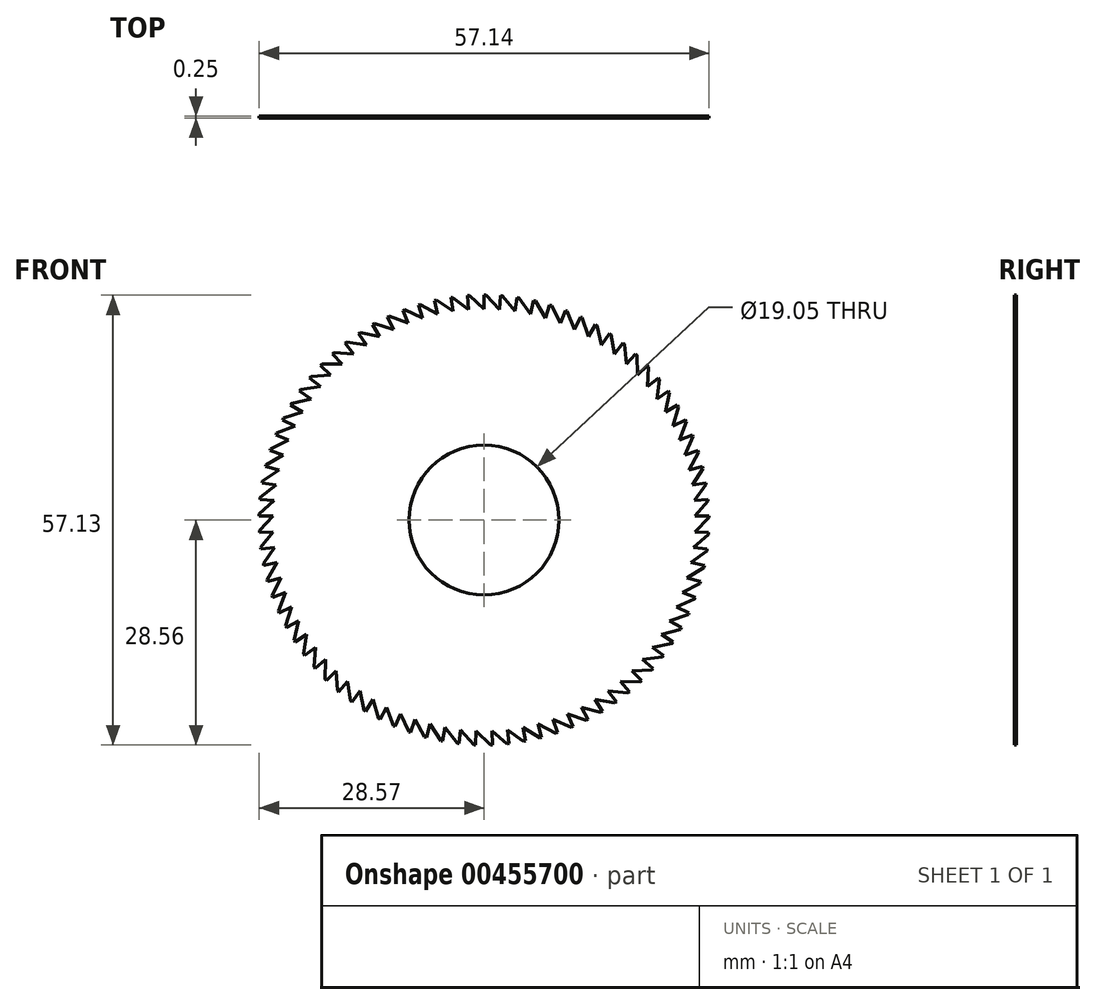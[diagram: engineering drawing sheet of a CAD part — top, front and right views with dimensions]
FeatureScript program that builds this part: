
annotation { "Feature Type Name" : "Feature", "Feature Type Description" : "" }
export const myFeature = defineFeature(function(context is Context, id is Id, definition is map)
    precondition{}
    {
        {
            var Q0;
            Q0=qCreatedBy(makeId("Front.planeOp"),FACE);
            var sketch = newSketch(context, id + "F0", { "sketchPlane" : qUnion([Q0])});
            skCircle(sketch, "E0", {"center": v(0, 0) * mm, "radius": 9.53 * mm});
            skLineSegment(sketch, "E1", {"start": v(0, 28.58) * mm, "end": v(0, 26.82) * mm});
            skLineSegment(sketch, "E2", {"start": v(0, 26.82) * mm, "end": v(-1.88, 28.51) * mm});
            skLineSegment(sketch, "E3.1.0", {"start": v(-1.98, 26.74) * mm, "end": v(-3.98, 28.3) * mm});
            skLineSegment(sketch, "E3.1.1", {"start": v(-2.11, 28.5) * mm, "end": v(-1.98, 26.74) * mm});
            skLineSegment(sketch, "E3.2.0", {"start": v(-3.95, 26.53) * mm, "end": v(-6.06, 27.93) * mm});
            skLineSegment(sketch, "E3.2.1", {"start": v(-4.2, 28.26) * mm, "end": v(-3.95, 26.53) * mm});
            skLineSegment(sketch, "E3.3.0", {"start": v(-5.9, 26.16) * mm, "end": v(-8.1, 27.4) * mm});
            skLineSegment(sketch, "E3.3.1", {"start": v(-6.28, 27.88) * mm, "end": v(-5.9, 26.16) * mm});
            skLineSegment(sketch, "E3.4.0", {"start": v(-7.81, 25.65) * mm, "end": v(-10.1, 26.73) * mm});
            skLineSegment(sketch, "E3.4.1", {"start": v(-8.33, 27.33) * mm, "end": v(-7.81, 25.65) * mm});
            skLineSegment(sketch, "E3.5.0", {"start": v(-9.69, 25) * mm, "end": v(-12.05, 25.9) * mm});
            skLineSegment(sketch, "E3.5.1", {"start": v(-10.32, 26.65) * mm, "end": v(-9.69, 25) * mm});
            skLineSegment(sketch, "E3.6.0", {"start": v(-11.5, 24.22) * mm, "end": v(-13.93, 24.95) * mm});
            skLineSegment(sketch, "E3.6.1", {"start": v(-12.26, 25.81) * mm, "end": v(-11.5, 24.22) * mm});
            skLineSegment(sketch, "E3.7.0", {"start": v(-13.27, 23.3) * mm, "end": v(-15.74, 23.85) * mm});
            skLineSegment(sketch, "E3.7.1", {"start": v(-14.13, 24.83) * mm, "end": v(-13.27, 23.3) * mm});
            skLineSegment(sketch, "E3.8.0", {"start": v(-14.95, 22.26) * mm, "end": v(-17.45, 22.62) * mm});
            skLineSegment(sketch, "E3.8.1", {"start": v(-15.93, 23.72) * mm, "end": v(-14.95, 22.26) * mm});
            skLineSegment(sketch, "E3.9.0", {"start": v(-16.55, 21.1) * mm, "end": v(-19.08, 21.27) * mm});
            skLineSegment(sketch, "E3.9.1", {"start": v(-17.64, 22.48) * mm, "end": v(-16.55, 21.1) * mm});
            skLineSegment(sketch, "E3.10.0", {"start": v(-18.07, 19.82) * mm, "end": v(-20.6, 19.8) * mm});
            skLineSegment(sketch, "E3.10.1", {"start": v(-19.25, 21.12) * mm, "end": v(-18.07, 19.82) * mm});
            skLineSegment(sketch, "E3.11.0", {"start": v(-19.48, 18.43) * mm, "end": v(-22, 18.23) * mm});
            skLineSegment(sketch, "E3.11.1", {"start": v(-20.76, 19.64) * mm, "end": v(-19.48, 18.43) * mm});
            skLineSegment(sketch, "E3.12.0", {"start": v(-20.79, 16.94) * mm, "end": v(-23.29, 16.56) * mm});
            skLineSegment(sketch, "E3.12.1", {"start": v(-22.15, 18.05) * mm, "end": v(-20.79, 16.94) * mm});
            skLineSegment(sketch, "E3.13.0", {"start": v(-21.98, 15.36) * mm, "end": v(-24.45, 14.8) * mm});
            skLineSegment(sketch, "E3.13.1", {"start": v(-23.42, 16.37) * mm, "end": v(-21.98, 15.36) * mm});
            skLineSegment(sketch, "E3.14.0", {"start": v(-23.06, 13.7) * mm, "end": v(-25.47, 12.95) * mm});
            skLineSegment(sketch, "E3.14.1", {"start": v(-24.57, 14.6) * mm, "end": v(-23.06, 13.7) * mm});
            skLineSegment(sketch, "E3.15.0", {"start": v(-24, 11.95) * mm, "end": v(-26.36, 11.03) * mm});
            skLineSegment(sketch, "E3.15.1", {"start": v(-25.58, 12.74) * mm, "end": v(-24, 11.95) * mm});
            skLineSegment(sketch, "E3.16.0", {"start": v(-24.82, 10.15) * mm, "end": v(-27.1, 9.05) * mm});
            skLineSegment(sketch, "E3.16.1", {"start": v(-26.45, 10.81) * mm, "end": v(-24.82, 10.15) * mm});
            skLineSegment(sketch, "E3.17.0", {"start": v(-25.5, 8.29) * mm, "end": v(-27.7, 7.03) * mm});
            skLineSegment(sketch, "E3.17.1", {"start": v(-27.18, 8.83) * mm, "end": v(-25.5, 8.29) * mm});
            skLineSegment(sketch, "E3.18.0", {"start": v(-26.05, 6.38) * mm, "end": v(-28.14, 4.96) * mm});
            skLineSegment(sketch, "E3.18.1", {"start": v(-27.75, 6.8) * mm, "end": v(-26.05, 6.38) * mm});
            skLineSegment(sketch, "E3.19.0", {"start": v(-26.45, 4.44) * mm, "end": v(-28.43, 2.87) * mm});
            skLineSegment(sketch, "E3.19.1", {"start": v(-28.18, 4.73) * mm, "end": v(-26.45, 4.44) * mm});
            skLineSegment(sketch, "E3.20.0", {"start": v(-26.7, 2.47) * mm, "end": v(-28.56, 0.76) * mm});
            skLineSegment(sketch, "E3.20.1", {"start": v(-28.45, 2.64) * mm, "end": v(-26.7, 2.47) * mm});
            skLineSegment(sketch, "E3.21.0", {"start": v(-26.81, 0.5) * mm, "end": v(-28.54, -1.35) * mm});
            skLineSegment(sketch, "E3.21.1", {"start": v(-28.57, 0.53) * mm, "end": v(-26.81, 0.5) * mm});
            skLineSegment(sketch, "E3.22.0", {"start": v(-26.78, -1.49) * mm, "end": v(-28.37, -3.45) * mm});
            skLineSegment(sketch, "E3.22.1", {"start": v(-28.53, -1.58) * mm, "end": v(-26.78, -1.49) * mm});
            skLineSegment(sketch, "E3.23.0", {"start": v(-26.6, -3.46) * mm, "end": v(-28.03, -5.54) * mm});
            skLineSegment(sketch, "E3.23.1", {"start": v(-28.34, -3.69) * mm, "end": v(-26.6, -3.46) * mm});
            skLineSegment(sketch, "E3.24.0", {"start": v(-26.27, -5.41) * mm, "end": v(-27.55, -7.6) * mm});
            skLineSegment(sketch, "E3.24.1", {"start": v(-27.99, -5.77) * mm, "end": v(-26.27, -5.41) * mm});
            skLineSegment(sketch, "E3.25.0", {"start": v(-25.8, -7.34) * mm, "end": v(-26.91, -9.6) * mm});
            skLineSegment(sketch, "E3.25.1", {"start": v(-27.48, -7.82) * mm, "end": v(-25.8, -7.34) * mm});
            skLineSegment(sketch, "E3.26.0", {"start": v(-25.18, -9.22) * mm, "end": v(-26.13, -11.57) * mm});
            skLineSegment(sketch, "E3.26.1", {"start": v(-26.83, -9.83) * mm, "end": v(-25.18, -9.22) * mm});
            skLineSegment(sketch, "E3.27.0", {"start": v(-24.43, -11.06) * mm, "end": v(-25.2, -13.47) * mm});
            skLineSegment(sketch, "E3.27.1", {"start": v(-26.03, -11.78) * mm, "end": v(-24.43, -11.06) * mm});
            skLineSegment(sketch, "E3.28.0", {"start": v(-23.55, -12.83) * mm, "end": v(-24.14, -15.3) * mm});
            skLineSegment(sketch, "E3.28.1", {"start": v(-25.1, -13.67) * mm, "end": v(-23.55, -12.83) * mm});
            skLineSegment(sketch, "E3.29.0", {"start": v(-22.54, -14.54) * mm, "end": v(-22.94, -17.03) * mm});
            skLineSegment(sketch, "E3.29.1", {"start": v(-24.01, -15.49) * mm, "end": v(-22.54, -14.54) * mm});
            skLineSegment(sketch, "E3.30.0", {"start": v(-21.4, -16.16) * mm, "end": v(-21.62, -18.68) * mm});
            skLineSegment(sketch, "E3.30.1", {"start": v(-22.8, -17.22) * mm, "end": v(-21.4, -16.16) * mm});
            skLineSegment(sketch, "E3.31.0", {"start": v(-20.15, -17.7) * mm, "end": v(-20.18, -20.23) * mm});
            skLineSegment(sketch, "E3.31.1", {"start": v(-21.47, -18.86) * mm, "end": v(-20.15, -17.7) * mm});
            skLineSegment(sketch, "E3.32.0", {"start": v(-18.79, -19.14) * mm, "end": v(-18.63, -21.66) * mm});
            skLineSegment(sketch, "E3.32.1", {"start": v(-20.02, -20.4) * mm, "end": v(-18.79, -19.14) * mm});
            skLineSegment(sketch, "E3.33.0", {"start": v(-17.32, -20.47) * mm, "end": v(-16.98, -22.98) * mm});
            skLineSegment(sketch, "E3.33.1", {"start": v(-18.46, -21.81) * mm, "end": v(-17.32, -20.47) * mm});
            skLineSegment(sketch, "E3.34.0", {"start": v(-15.76, -21.7) * mm, "end": v(-15.24, -24.17) * mm});
            skLineSegment(sketch, "E3.34.1", {"start": v(-16.8, -23.12) * mm, "end": v(-15.76, -21.7) * mm});
            skLineSegment(sketch, "E3.35.0", {"start": v(-14.12, -22.8) * mm, "end": v(-13.41, -25.23) * mm});
            skLineSegment(sketch, "E3.35.1", {"start": v(-15.04, -24.3) * mm, "end": v(-14.12, -22.8) * mm});
            skLineSegment(sketch, "E3.36.0", {"start": v(-12.4, -23.78) * mm, "end": v(-11.51, -26.15) * mm});
            skLineSegment(sketch, "E3.36.1", {"start": v(-13.2, -25.34) * mm, "end": v(-12.4, -23.78) * mm});
            skLineSegment(sketch, "E3.37.0", {"start": v(-10.6, -24.63) * mm, "end": v(-9.55, -26.93) * mm});
            skLineSegment(sketch, "E3.37.1", {"start": v(-11.3, -26.25) * mm, "end": v(-10.6, -24.63) * mm});
            skLineSegment(sketch, "E3.38.0", {"start": v(-8.76, -25.35) * mm, "end": v(-7.54, -27.56) * mm});
            skLineSegment(sketch, "E3.38.1", {"start": v(-9.33, -27) * mm, "end": v(-8.76, -25.35) * mm});
            skLineSegment(sketch, "E3.39.0", {"start": v(-6.86, -25.93) * mm, "end": v(-5.48, -28.04) * mm});
            skLineSegment(sketch, "E3.39.1", {"start": v(-7.31, -27.62) * mm, "end": v(-6.86, -25.93) * mm});
            skLineSegment(sketch, "E3.40.0", {"start": v(-4.93, -26.36) * mm, "end": v(-3.4, -28.37) * mm});
            skLineSegment(sketch, "E3.40.1", {"start": v(-5.25, -28.09) * mm, "end": v(-4.93, -26.36) * mm});
            skLineSegment(sketch, "E3.41.0", {"start": v(-2.97, -26.65) * mm, "end": v(-1.29, -28.55) * mm});
            skLineSegment(sketch, "E3.41.1", {"start": v(-3.16, -28.4) * mm, "end": v(-2.97, -26.65) * mm});
            skLineSegment(sketch, "E3.42.0", {"start": v(-1, -26.8) * mm, "end": v(0.82, -28.56) * mm});
            skLineSegment(sketch, "E3.42.1", {"start": v(-1.06, -28.56) * mm, "end": v(-1, -26.8) * mm});
            skLineSegment(sketch, "E3.43.0", {"start": v(1, -26.8) * mm, "end": v(2.93, -28.42) * mm});
            skLineSegment(sketch, "E3.43.1", {"start": v(1.06, -28.56) * mm, "end": v(1, -26.8) * mm});
            skLineSegment(sketch, "E3.44.0", {"start": v(2.97, -26.65) * mm, "end": v(5.02, -28.13) * mm});
            skLineSegment(sketch, "E3.44.1", {"start": v(3.16, -28.4) * mm, "end": v(2.97, -26.65) * mm});
            skLineSegment(sketch, "E3.45.0", {"start": v(4.93, -26.36) * mm, "end": v(7.09, -27.68) * mm});
            skLineSegment(sketch, "E3.45.1", {"start": v(5.25, -28.09) * mm, "end": v(4.93, -26.36) * mm});
            skLineSegment(sketch, "E3.46.0", {"start": v(6.86, -25.93) * mm, "end": v(9.11, -27.08) * mm});
            skLineSegment(sketch, "E3.46.1", {"start": v(7.31, -27.62) * mm, "end": v(6.86, -25.93) * mm});
            skLineSegment(sketch, "E3.47.0", {"start": v(8.76, -25.35) * mm, "end": v(11.09, -26.34) * mm});
            skLineSegment(sketch, "E3.47.1", {"start": v(9.33, -27) * mm, "end": v(8.76, -25.35) * mm});
            skLineSegment(sketch, "E3.48.0", {"start": v(10.6, -24.63) * mm, "end": v(13, -25.45) * mm});
            skLineSegment(sketch, "E3.48.1", {"start": v(11.3, -26.25) * mm, "end": v(10.6, -24.63) * mm});
            skLineSegment(sketch, "E3.49.0", {"start": v(12.4, -23.78) * mm, "end": v(14.84, -24.42) * mm});
            skLineSegment(sketch, "E3.49.1", {"start": v(13.2, -25.34) * mm, "end": v(12.4, -23.78) * mm});
            skLineSegment(sketch, "E3.50.0", {"start": v(14.12, -22.8) * mm, "end": v(16.6, -23.25) * mm});
            skLineSegment(sketch, "E3.50.1", {"start": v(15.04, -24.3) * mm, "end": v(14.12, -22.8) * mm});
            skLineSegment(sketch, "E3.51.0", {"start": v(15.76, -21.7) * mm, "end": v(18.28, -21.96) * mm});
            skLineSegment(sketch, "E3.51.1", {"start": v(16.8, -23.12) * mm, "end": v(15.76, -21.7) * mm});
            skLineSegment(sketch, "E3.52.0", {"start": v(17.32, -20.47) * mm, "end": v(19.85, -20.55) * mm});
            skLineSegment(sketch, "E3.52.1", {"start": v(18.46, -21.81) * mm, "end": v(17.32, -20.47) * mm});
            skLineSegment(sketch, "E3.53.0", {"start": v(18.79, -19.14) * mm, "end": v(21.31, -19.03) * mm});
            skLineSegment(sketch, "E3.53.1", {"start": v(20.02, -20.4) * mm, "end": v(18.79, -19.14) * mm});
            skLineSegment(sketch, "E3.54.0", {"start": v(20.15, -17.7) * mm, "end": v(22.66, -17.4) * mm});
            skLineSegment(sketch, "E3.54.1", {"start": v(21.47, -18.86) * mm, "end": v(20.15, -17.7) * mm});
            skLineSegment(sketch, "E3.55.0", {"start": v(21.4, -16.16) * mm, "end": v(23.89, -15.68) * mm});
            skLineSegment(sketch, "E3.55.1", {"start": v(22.8, -17.22) * mm, "end": v(21.4, -16.16) * mm});
            skLineSegment(sketch, "E3.56.0", {"start": v(22.54, -14.54) * mm, "end": v(24.98, -13.88) * mm});
            skLineSegment(sketch, "E3.56.1", {"start": v(24.01, -15.49) * mm, "end": v(22.54, -14.54) * mm});
            skLineSegment(sketch, "E3.57.0", {"start": v(23.55, -12.83) * mm, "end": v(25.94, -12) * mm});
            skLineSegment(sketch, "E3.57.1", {"start": v(25.1, -13.67) * mm, "end": v(23.55, -12.83) * mm});
            skLineSegment(sketch, "E3.58.0", {"start": v(24.43, -11.06) * mm, "end": v(26.75, -10.05) * mm});
            skLineSegment(sketch, "E3.58.1", {"start": v(26.03, -11.78) * mm, "end": v(24.43, -11.06) * mm});
            skLineSegment(sketch, "E3.59.0", {"start": v(25.18, -9.22) * mm, "end": v(27.42, -8.04) * mm});
            skLineSegment(sketch, "E3.59.1", {"start": v(26.83, -9.83) * mm, "end": v(25.18, -9.22) * mm});
            skLineSegment(sketch, "E3.60.0", {"start": v(25.8, -7.34) * mm, "end": v(27.94, -6) * mm});
            skLineSegment(sketch, "E3.60.1", {"start": v(27.48, -7.82) * mm, "end": v(25.8, -7.34) * mm});
            skLineSegment(sketch, "E3.61.0", {"start": v(26.27, -5.41) * mm, "end": v(28.3, -3.92) * mm});
            skLineSegment(sketch, "E3.61.1", {"start": v(27.99, -5.77) * mm, "end": v(26.27, -5.41) * mm});
            skLineSegment(sketch, "E3.62.0", {"start": v(26.6, -3.46) * mm, "end": v(28.52, -1.82) * mm});
            skLineSegment(sketch, "E3.62.1", {"start": v(28.34, -3.69) * mm, "end": v(26.6, -3.46) * mm});
            skLineSegment(sketch, "E3.63.0", {"start": v(26.78, -1.49) * mm, "end": v(28.57, 0.3) * mm});
            skLineSegment(sketch, "E3.63.1", {"start": v(28.53, -1.58) * mm, "end": v(26.78, -1.49) * mm});
            skLineSegment(sketch, "E3.64.0", {"start": v(26.81, 0.5) * mm, "end": v(28.47, 2.4) * mm});
            skLineSegment(sketch, "E3.64.1", {"start": v(28.57, 0.53) * mm, "end": v(26.81, 0.5) * mm});
            skLineSegment(sketch, "E3.65.0", {"start": v(26.7, 2.47) * mm, "end": v(28.22, 4.5) * mm});
            skLineSegment(sketch, "E3.65.1", {"start": v(28.45, 2.64) * mm, "end": v(26.7, 2.47) * mm});
            skLineSegment(sketch, "E3.66.0", {"start": v(26.45, 4.44) * mm, "end": v(27.8, 6.57) * mm});
            skLineSegment(sketch, "E3.66.1", {"start": v(28.18, 4.73) * mm, "end": v(26.45, 4.44) * mm});
            skLineSegment(sketch, "E3.67.0", {"start": v(26.05, 6.38) * mm, "end": v(27.25, 8.6) * mm});
            skLineSegment(sketch, "E3.67.1", {"start": v(27.75, 6.8) * mm, "end": v(26.05, 6.38) * mm});
            skLineSegment(sketch, "E3.68.0", {"start": v(25.5, 8.29) * mm, "end": v(26.54, 10.6) * mm});
            skLineSegment(sketch, "E3.68.1", {"start": v(27.18, 8.83) * mm, "end": v(25.5, 8.29) * mm});
            skLineSegment(sketch, "E3.69.0", {"start": v(24.82, 10.15) * mm, "end": v(25.68, 12.53) * mm});
            skLineSegment(sketch, "E3.69.1", {"start": v(26.45, 10.81) * mm, "end": v(24.82, 10.15) * mm});
            skLineSegment(sketch, "E3.70.0", {"start": v(24, 11.95) * mm, "end": v(24.69, 14.4) * mm});
            skLineSegment(sketch, "E3.70.1", {"start": v(25.58, 12.74) * mm, "end": v(24, 11.95) * mm});
            skLineSegment(sketch, "E3.71.0", {"start": v(23.06, 13.7) * mm, "end": v(23.56, 16.17) * mm});
            skLineSegment(sketch, "E3.71.1", {"start": v(24.57, 14.6) * mm, "end": v(23.06, 13.7) * mm});
            skLineSegment(sketch, "E3.72.0", {"start": v(21.98, 15.36) * mm, "end": v(22.3, 17.87) * mm});
            skLineSegment(sketch, "E3.72.1", {"start": v(23.42, 16.37) * mm, "end": v(21.98, 15.36) * mm});
            skLineSegment(sketch, "E3.73.0", {"start": v(20.79, 16.94) * mm, "end": v(20.92, 19.47) * mm});
            skLineSegment(sketch, "E3.73.1", {"start": v(22.15, 18.05) * mm, "end": v(20.79, 16.94) * mm});
            skLineSegment(sketch, "E3.74.0", {"start": v(19.48, 18.43) * mm, "end": v(19.42, 20.96) * mm});
            skLineSegment(sketch, "E3.74.1", {"start": v(20.76, 19.64) * mm, "end": v(19.48, 18.43) * mm});
            skLineSegment(sketch, "E3.75.0", {"start": v(18.07, 19.82) * mm, "end": v(17.82, 22.34) * mm});
            skLineSegment(sketch, "E3.75.1", {"start": v(19.25, 21.12) * mm, "end": v(18.07, 19.82) * mm});
            skLineSegment(sketch, "E3.76.0", {"start": v(16.55, 21.1) * mm, "end": v(16.12, 23.6) * mm});
            skLineSegment(sketch, "E3.76.1", {"start": v(17.64, 22.48) * mm, "end": v(16.55, 21.1) * mm});
            skLineSegment(sketch, "E3.77.0", {"start": v(14.95, 22.26) * mm, "end": v(14.34, 24.72) * mm});
            skLineSegment(sketch, "E3.77.1", {"start": v(15.93, 23.72) * mm, "end": v(14.95, 22.26) * mm});
            skLineSegment(sketch, "E3.78.0", {"start": v(13.27, 23.3) * mm, "end": v(12.47, 25.7) * mm});
            skLineSegment(sketch, "E3.78.1", {"start": v(14.13, 24.83) * mm, "end": v(13.27, 23.3) * mm});
            skLineSegment(sketch, "E3.79.0", {"start": v(11.5, 24.22) * mm, "end": v(10.54, 26.56) * mm});
            skLineSegment(sketch, "E3.79.1", {"start": v(12.26, 25.81) * mm, "end": v(11.5, 24.22) * mm});
            skLineSegment(sketch, "E3.80.0", {"start": v(9.69, 25) * mm, "end": v(8.55, 27.27) * mm});
            skLineSegment(sketch, "E3.80.1", {"start": v(10.32, 26.65) * mm, "end": v(9.69, 25) * mm});
            skLineSegment(sketch, "E3.81.0", {"start": v(7.81, 25.65) * mm, "end": v(6.51, 27.82) * mm});
            skLineSegment(sketch, "E3.81.1", {"start": v(8.33, 27.33) * mm, "end": v(7.81, 25.65) * mm});
            skLineSegment(sketch, "E3.82.0", {"start": v(5.9, 26.16) * mm, "end": v(4.44, 28.23) * mm});
            skLineSegment(sketch, "E3.82.1", {"start": v(6.28, 27.88) * mm, "end": v(5.9, 26.16) * mm});
            skLineSegment(sketch, "E3.83.0", {"start": v(3.95, 26.53) * mm, "end": v(2.34, 28.48) * mm});
            skLineSegment(sketch, "E3.83.1", {"start": v(4.2, 28.26) * mm, "end": v(3.95, 26.53) * mm});
            skLineSegment(sketch, "E3.84.0", {"start": v(1.98, 26.74) * mm, "end": v(0.23, 28.57) * mm});
            skLineSegment(sketch, "E3.84.1", {"start": v(2.11, 28.5) * mm, "end": v(1.98, 26.74) * mm});
            skLineSegment(sketch, "E4", {"start": v(0, 28.58) * mm, "end": v(0.23, 28.57) * mm});
            skLineSegment(sketch, "E5.1.0", {"start": v(-2.11, 28.5) * mm, "end": v(-1.88, 28.51) * mm});
            skLineSegment(sketch, "E5.2.0", {"start": v(-4.2, 28.26) * mm, "end": v(-3.98, 28.3) * mm});
            skLineSegment(sketch, "E5.3.0", {"start": v(-6.28, 27.88) * mm, "end": v(-6.06, 27.93) * mm});
            skLineSegment(sketch, "E5.4.0", {"start": v(-8.33, 27.33) * mm, "end": v(-8.1, 27.4) * mm});
            skLineSegment(sketch, "E5.5.0", {"start": v(-10.32, 26.65) * mm, "end": v(-10.1, 26.73) * mm});
            skLineSegment(sketch, "E5.6.0", {"start": v(-12.26, 25.81) * mm, "end": v(-12.05, 25.9) * mm});
            skLineSegment(sketch, "E5.7.0", {"start": v(-14.13, 24.83) * mm, "end": v(-13.93, 24.95) * mm});
            skLineSegment(sketch, "E5.8.0", {"start": v(-15.93, 23.72) * mm, "end": v(-15.74, 23.85) * mm});
            skLineSegment(sketch, "E5.9.0", {"start": v(-17.64, 22.48) * mm, "end": v(-17.45, 22.62) * mm});
            skLineSegment(sketch, "E5.10.0", {"start": v(-19.25, 21.12) * mm, "end": v(-19.08, 21.27) * mm});
            skLineSegment(sketch, "E5.11.0", {"start": v(-20.76, 19.64) * mm, "end": v(-20.6, 19.8) * mm});
            skLineSegment(sketch, "E5.12.0", {"start": v(-22.15, 18.05) * mm, "end": v(-22, 18.23) * mm});
            skLineSegment(sketch, "E5.13.0", {"start": v(-23.42, 16.37) * mm, "end": v(-23.29, 16.56) * mm});
            skLineSegment(sketch, "E5.14.0", {"start": v(-24.57, 14.6) * mm, "end": v(-24.45, 14.8) * mm});
            skLineSegment(sketch, "E5.15.0", {"start": v(-25.58, 12.74) * mm, "end": v(-25.47, 12.95) * mm});
            skLineSegment(sketch, "E5.16.0", {"start": v(-26.45, 10.81) * mm, "end": v(-26.36, 11.03) * mm});
            skLineSegment(sketch, "E5.17.0", {"start": v(-27.18, 8.83) * mm, "end": v(-27.1, 9.05) * mm});
            skLineSegment(sketch, "E5.18.0", {"start": v(-27.75, 6.8) * mm, "end": v(-27.7, 7.03) * mm});
            skLineSegment(sketch, "E5.19.0", {"start": v(-28.18, 4.73) * mm, "end": v(-28.14, 4.96) * mm});
            skLineSegment(sketch, "E5.20.0", {"start": v(-28.45, 2.64) * mm, "end": v(-28.43, 2.87) * mm});
            skLineSegment(sketch, "E5.21.0", {"start": v(-28.57, 0.53) * mm, "end": v(-28.56, 0.76) * mm});
            skLineSegment(sketch, "E5.22.0", {"start": v(-28.53, -1.58) * mm, "end": v(-28.54, -1.35) * mm});
            skLineSegment(sketch, "E5.23.0", {"start": v(-28.34, -3.69) * mm, "end": v(-28.37, -3.45) * mm});
            skLineSegment(sketch, "E5.24.0", {"start": v(-27.99, -5.77) * mm, "end": v(-28.03, -5.54) * mm});
            skLineSegment(sketch, "E5.25.0", {"start": v(-27.48, -7.82) * mm, "end": v(-27.55, -7.6) * mm});
            skLineSegment(sketch, "E5.26.0", {"start": v(-26.83, -9.83) * mm, "end": v(-26.91, -9.6) * mm});
            skLineSegment(sketch, "E5.27.0", {"start": v(-26.03, -11.78) * mm, "end": v(-26.13, -11.57) * mm});
            skLineSegment(sketch, "E5.28.0", {"start": v(-25.1, -13.67) * mm, "end": v(-25.2, -13.47) * mm});
            skLineSegment(sketch, "E5.29.0", {"start": v(-24.01, -15.49) * mm, "end": v(-24.14, -15.3) * mm});
            skLineSegment(sketch, "E5.30.0", {"start": v(-22.8, -17.22) * mm, "end": v(-22.94, -17.03) * mm});
            skLineSegment(sketch, "E5.31.0", {"start": v(-21.47, -18.86) * mm, "end": v(-21.62, -18.68) * mm});
            skLineSegment(sketch, "E5.32.0", {"start": v(-20.02, -20.4) * mm, "end": v(-20.18, -20.23) * mm});
            skLineSegment(sketch, "E5.33.0", {"start": v(-18.46, -21.81) * mm, "end": v(-18.63, -21.66) * mm});
            skLineSegment(sketch, "E5.34.0", {"start": v(-16.8, -23.12) * mm, "end": v(-16.98, -22.98) * mm});
            skLineSegment(sketch, "E5.35.0", {"start": v(-15.04, -24.3) * mm, "end": v(-15.24, -24.17) * mm});
            skLineSegment(sketch, "E5.36.0", {"start": v(-13.2, -25.34) * mm, "end": v(-13.41, -25.23) * mm});
            skLineSegment(sketch, "E5.37.0", {"start": v(-11.3, -26.25) * mm, "end": v(-11.51, -26.15) * mm});
            skLineSegment(sketch, "E5.38.0", {"start": v(-9.33, -27) * mm, "end": v(-9.55, -26.93) * mm});
            skLineSegment(sketch, "E5.39.0", {"start": v(-7.31, -27.62) * mm, "end": v(-7.54, -27.56) * mm});
            skLineSegment(sketch, "E5.40.0", {"start": v(-5.25, -28.09) * mm, "end": v(-5.48, -28.04) * mm});
            skLineSegment(sketch, "E5.41.0", {"start": v(-3.16, -28.4) * mm, "end": v(-3.4, -28.37) * mm});
            skLineSegment(sketch, "E5.42.0", {"start": v(-1.06, -28.56) * mm, "end": v(-1.29, -28.55) * mm});
            skLineSegment(sketch, "E5.43.0", {"start": v(1.06, -28.56) * mm, "end": v(0.82, -28.56) * mm});
            skLineSegment(sketch, "E5.44.0", {"start": v(3.16, -28.4) * mm, "end": v(2.93, -28.42) * mm});
            skLineSegment(sketch, "E5.45.0", {"start": v(5.25, -28.09) * mm, "end": v(5.02, -28.13) * mm});
            skLineSegment(sketch, "E5.46.0", {"start": v(7.31, -27.62) * mm, "end": v(7.09, -27.68) * mm});
            skLineSegment(sketch, "E5.47.0", {"start": v(9.33, -27) * mm, "end": v(9.11, -27.08) * mm});
            skLineSegment(sketch, "E5.48.0", {"start": v(11.3, -26.25) * mm, "end": v(11.09, -26.34) * mm});
            skLineSegment(sketch, "E5.49.0", {"start": v(13.2, -25.34) * mm, "end": v(13, -25.45) * mm});
            skLineSegment(sketch, "E5.50.0", {"start": v(15.04, -24.3) * mm, "end": v(14.84, -24.42) * mm});
            skLineSegment(sketch, "E5.51.0", {"start": v(16.8, -23.12) * mm, "end": v(16.6, -23.25) * mm});
            skLineSegment(sketch, "E5.52.0", {"start": v(18.46, -21.81) * mm, "end": v(18.28, -21.96) * mm});
            skLineSegment(sketch, "E5.53.0", {"start": v(20.02, -20.4) * mm, "end": v(19.85, -20.55) * mm});
            skLineSegment(sketch, "E5.54.0", {"start": v(21.47, -18.86) * mm, "end": v(21.31, -19.03) * mm});
            skLineSegment(sketch, "E5.55.0", {"start": v(22.8, -17.22) * mm, "end": v(22.66, -17.4) * mm});
            skLineSegment(sketch, "E5.56.0", {"start": v(24.01, -15.49) * mm, "end": v(23.89, -15.68) * mm});
            skLineSegment(sketch, "E5.57.0", {"start": v(25.1, -13.67) * mm, "end": v(24.98, -13.88) * mm});
            skLineSegment(sketch, "E5.58.0", {"start": v(26.03, -11.78) * mm, "end": v(25.94, -12) * mm});
            skLineSegment(sketch, "E5.59.0", {"start": v(26.83, -9.83) * mm, "end": v(26.75, -10.05) * mm});
            skLineSegment(sketch, "E5.60.0", {"start": v(27.48, -7.82) * mm, "end": v(27.42, -8.04) * mm});
            skLineSegment(sketch, "E5.61.0", {"start": v(27.99, -5.77) * mm, "end": v(27.94, -6) * mm});
            skLineSegment(sketch, "E5.62.0", {"start": v(28.34, -3.69) * mm, "end": v(28.3, -3.92) * mm});
            skLineSegment(sketch, "E5.63.0", {"start": v(28.53, -1.58) * mm, "end": v(28.52, -1.82) * mm});
            skLineSegment(sketch, "E5.64.0", {"start": v(28.57, 0.53) * mm, "end": v(28.57, 0.3) * mm});
            skLineSegment(sketch, "E5.65.0", {"start": v(28.45, 2.64) * mm, "end": v(28.47, 2.4) * mm});
            skLineSegment(sketch, "E5.66.0", {"start": v(28.18, 4.73) * mm, "end": v(28.22, 4.5) * mm});
            skLineSegment(sketch, "E5.67.0", {"start": v(27.75, 6.8) * mm, "end": v(27.8, 6.57) * mm});
            skLineSegment(sketch, "E5.68.0", {"start": v(27.18, 8.83) * mm, "end": v(27.25, 8.6) * mm});
            skLineSegment(sketch, "E5.69.0", {"start": v(26.45, 10.81) * mm, "end": v(26.54, 10.6) * mm});
            skLineSegment(sketch, "E5.70.0", {"start": v(25.58, 12.74) * mm, "end": v(25.68, 12.53) * mm});
            skLineSegment(sketch, "E5.71.0", {"start": v(24.57, 14.6) * mm, "end": v(24.69, 14.4) * mm});
            skLineSegment(sketch, "E5.72.0", {"start": v(23.42, 16.37) * mm, "end": v(23.56, 16.17) * mm});
            skLineSegment(sketch, "E5.73.0", {"start": v(22.15, 18.05) * mm, "end": v(22.3, 17.87) * mm});
            skLineSegment(sketch, "E5.74.0", {"start": v(20.76, 19.64) * mm, "end": v(20.92, 19.47) * mm});
            skLineSegment(sketch, "E5.75.0", {"start": v(19.25, 21.12) * mm, "end": v(19.42, 20.96) * mm});
            skLineSegment(sketch, "E5.76.0", {"start": v(17.64, 22.48) * mm, "end": v(17.82, 22.34) * mm});
            skLineSegment(sketch, "E5.77.0", {"start": v(15.93, 23.72) * mm, "end": v(16.12, 23.6) * mm});
            skLineSegment(sketch, "E5.78.0", {"start": v(14.13, 24.83) * mm, "end": v(14.34, 24.72) * mm});
            skLineSegment(sketch, "E5.79.0", {"start": v(12.26, 25.81) * mm, "end": v(12.47, 25.7) * mm});
            skLineSegment(sketch, "E5.80.0", {"start": v(10.32, 26.65) * mm, "end": v(10.54, 26.56) * mm});
            skLineSegment(sketch, "E5.81.0", {"start": v(8.33, 27.33) * mm, "end": v(8.55, 27.27) * mm});
            skLineSegment(sketch, "E5.82.0", {"start": v(6.28, 27.88) * mm, "end": v(6.51, 27.82) * mm});
            skLineSegment(sketch, "E5.83.0", {"start": v(4.2, 28.26) * mm, "end": v(4.44, 28.23) * mm});
            skLineSegment(sketch, "E5.84.0", {"start": v(2.11, 28.5) * mm, "end": v(2.34, 28.48) * mm});
            skSolve(sketch);
        }
        {
            var Q0;
            Q0=makeQuery(id+"F0.imprint","IMPRINT",FACE,{"disambiguationData":[TD([[makeQuery(id+"F0.imprint","IMPRINT",EDGE,{"derivedFrom":sQuery(id+"F0.wireOp",EDGE,"E0")}),-1.0]])]});
            extrude(context, id + "F1", {"entities" : qUnion([Q0]), "depth" : 0.25 * mm});
        }
    });
